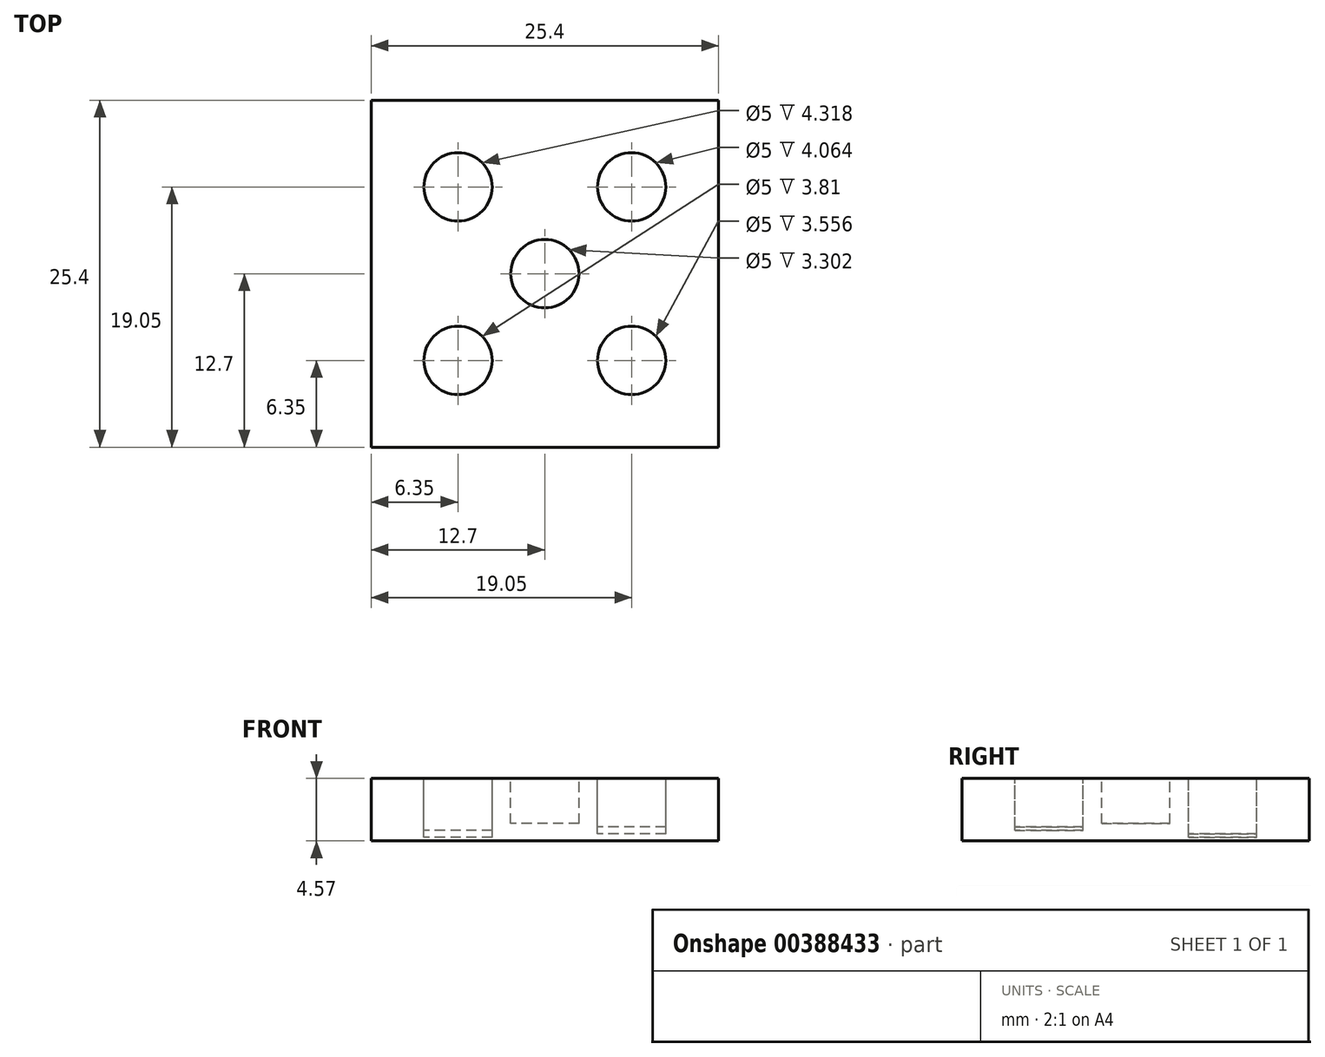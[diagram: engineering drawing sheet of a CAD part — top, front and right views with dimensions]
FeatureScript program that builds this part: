
annotation { "Feature Type Name" : "Feature", "Feature Type Description" : "" }
export const myFeature = defineFeature(function(context is Context, id is Id, definition is map)
    precondition{}
    {
        {
            var Q0;
            Q0=qCreatedBy(makeId("Top.planeOp"),FACE);
            var sketch = newSketch(context, id + "F0", { "sketchPlane" : qUnion([Q0])});
            skLineSegment(sketch, "E0.bottom", {"start": v(12.7, -12.7) * mm, "end": v(-12.7, -12.7) * mm});
            skLineSegment(sketch, "E0.top", {"start": v(12.7, 12.7) * mm, "end": v(-12.7, 12.7) * mm});
            skLineSegment(sketch, "E0.left", {"start": v(12.7, -12.7) * mm, "end": v(12.7, 12.7) * mm});
            skLineSegment(sketch, "E0.right", {"start": v(-12.7, -12.7) * mm, "end": v(-12.7, 12.7) * mm});
            skPoint(sketch, "E0.middle", {"position": v(0, 0) * mm});
            skSolve(sketch);
        }
        {
            var Q0;
            Q0 = qSketchRegion(id + "F0", true);
            extrude(context, id + "F1", {"entities" : qUnion([Q0]), "depth" : 4.57 * mm});
        }
        {
            var Q0;
            Q0=makeQuery(id+"F1.opExtrude","CAP_FACE",FACE,{"disambiguationData":[OSD([sQuery(id+"F0.wireOp",EDGE,"E0.bottom"),sQuery(id+"F0.wireOp",EDGE,"E0.top"),sQuery(id+"F0.wireOp",EDGE,"E0.left"),sQuery(id+"F0.wireOp",EDGE,"E0.right")])],"isStart":false});
            var sketch = newSketch(context, id + "F2", { "sketchPlane" : qUnion([Q0])});
            skCircle(sketch, "E1", {"center": v(-6.35, 6.35) * mm, "radius": 2.5 * mm});
            skSolve(sketch);
        }
        {
            var Q0;
            Q0=makeQuery(id+"F2.imprint","IMPRINT",FACE,{"disambiguationData":[TD([[makeQuery(id+"F2.imprint","IMPRINT",EDGE,{"derivedFrom":sQuery(id+"F2.wireOp",EDGE,"E1")}),1.0]])]});
            extrude(context, id + "F3", {"entities" : qUnion([Q0]), "operationType" : NewBodyOperationType.REMOVE, "oppositeDirection" : true, "depth" : 4.32 * mm});
        }
        {
            var Q0;
            Q0=makeQuery(id+"F1.opExtrude","CAP_FACE",FACE,{"disambiguationData":[OSD([sQuery(id+"F0.wireOp",EDGE,"E0.bottom"),sQuery(id+"F0.wireOp",EDGE,"E0.top"),sQuery(id+"F0.wireOp",EDGE,"E0.left"),sQuery(id+"F0.wireOp",EDGE,"E0.right")])],"isStart":false});
            var sketch = newSketch(context, id + "F4", { "sketchPlane" : qUnion([Q0])});
            skCircle(sketch, "E2", {"center": v(6.35, 6.35) * mm, "radius": 2.5 * mm});
            skSolve(sketch);
        }
        {
            var Q0;
            Q0=makeQuery(id+"F4.imprint","IMPRINT",FACE,{"disambiguationData":[TD([[makeQuery(id+"F4.imprint","IMPRINT",EDGE,{"derivedFrom":sQuery(id+"F4.wireOp",EDGE,"E2")}),1.0]])]});
            extrude(context, id + "F5", {"entities" : qUnion([Q0]), "operationType" : NewBodyOperationType.REMOVE, "oppositeDirection" : true, "depth" : 4.06 * mm});
        }
        {
            var Q0;
            Q0=makeQuery(id+"F1.opExtrude","CAP_FACE",FACE,{"disambiguationData":[OSD([sQuery(id+"F0.wireOp",EDGE,"E0.bottom"),sQuery(id+"F0.wireOp",EDGE,"E0.top"),sQuery(id+"F0.wireOp",EDGE,"E0.left"),sQuery(id+"F0.wireOp",EDGE,"E0.right")])],"isStart":false});
            var sketch = newSketch(context, id + "F6", { "sketchPlane" : qUnion([Q0])});
            skCircle(sketch, "E3", {"center": v(-6.35, -6.35) * mm, "radius": 2.5 * mm});
            skSolve(sketch);
        }
        {
            var Q0;
            Q0=makeQuery(id+"F6.imprint","IMPRINT",FACE,{"disambiguationData":[TD([[makeQuery(id+"F6.imprint","IMPRINT",EDGE,{"derivedFrom":sQuery(id+"F6.wireOp",EDGE,"E3")}),1.0]])]});
            extrude(context, id + "F7", {"entities" : qUnion([Q0]), "operationType" : NewBodyOperationType.REMOVE, "oppositeDirection" : true, "depth" : 3.8 * mm});
        }
        {
            var Q0;
            Q0=makeQuery(id+"F1.opExtrude","CAP_FACE",FACE,{"disambiguationData":[OSD([sQuery(id+"F0.wireOp",EDGE,"E0.bottom"),sQuery(id+"F0.wireOp",EDGE,"E0.top"),sQuery(id+"F0.wireOp",EDGE,"E0.left"),sQuery(id+"F0.wireOp",EDGE,"E0.right")])],"isStart":false});
            var sketch = newSketch(context, id + "F8", { "sketchPlane" : qUnion([Q0])});
            skCircle(sketch, "E4", {"center": v(6.35, -6.35) * mm, "radius": 2.5 * mm});
            skSolve(sketch);
        }
        {
            var Q0;
            Q0=makeQuery(id+"F8.imprint","IMPRINT",FACE,{"disambiguationData":[TD([[makeQuery(id+"F8.imprint","IMPRINT",EDGE,{"derivedFrom":sQuery(id+"F8.wireOp",EDGE,"E4")}),1.0]])]});
            extrude(context, id + "F9", {"entities" : qUnion([Q0]), "operationType" : NewBodyOperationType.REMOVE, "oppositeDirection" : true, "depth" : 3.56 * mm});
        }
        {
            var Q0;
            Q0=makeQuery(id+"F1.opExtrude","CAP_FACE",FACE,{"disambiguationData":[OSD([sQuery(id+"F0.wireOp",EDGE,"E0.bottom"),sQuery(id+"F0.wireOp",EDGE,"E0.top"),sQuery(id+"F0.wireOp",EDGE,"E0.left"),sQuery(id+"F0.wireOp",EDGE,"E0.right")])],"isStart":false});
            var sketch = newSketch(context, id + "F10", { "sketchPlane" : qUnion([Q0])});
            skCircle(sketch, "E5", {"center": v(0, 0) * mm, "radius": 2.5 * mm});
            skSolve(sketch);
        }
        {
            var Q0;
            Q0 = qSketchRegion(id + "F10", true);
            extrude(context, id + "F11", {"entities" : qUnion([Q0]), "operationType" : NewBodyOperationType.REMOVE, "oppositeDirection" : true, "depth" : 3.3 * mm});
        }
    });
